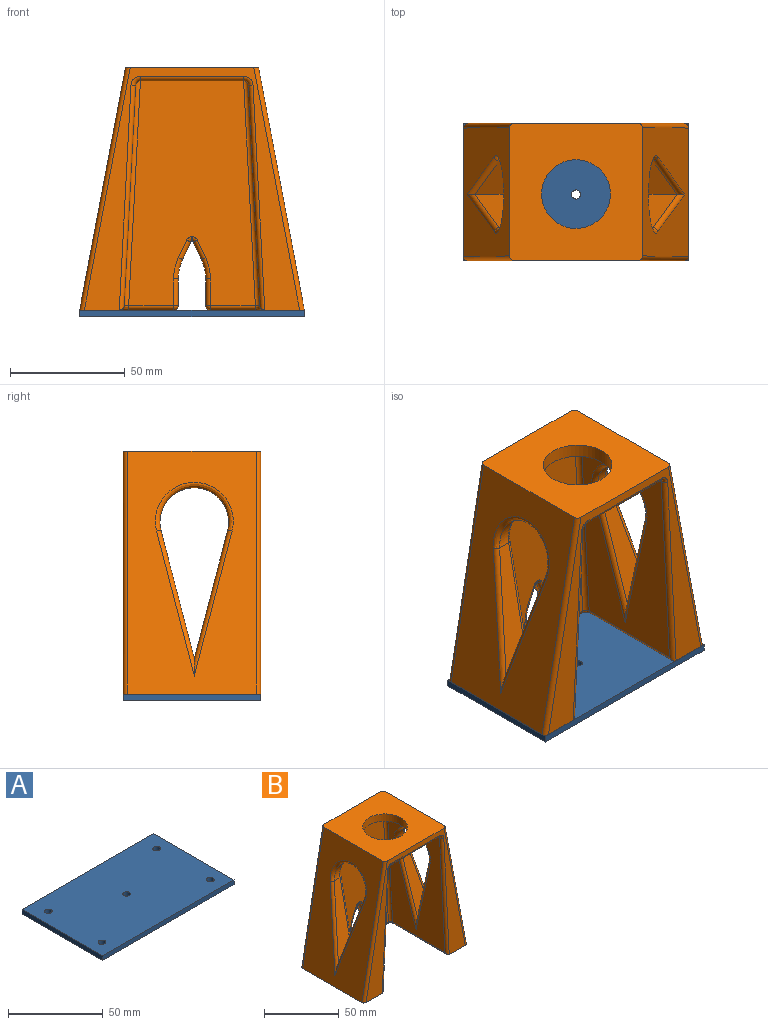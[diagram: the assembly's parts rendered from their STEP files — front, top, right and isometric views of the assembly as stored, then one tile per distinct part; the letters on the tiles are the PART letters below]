
ASSEMBLY  parts=2 mates=1
PART A: 11 faces, bbox 98x60x3 mm
  f0: plane 98x3mm, normal (0,-1,0), area 294mm2, adj f1,f3,f4,f5
  f1: plane 60x3mm, normal (1,0,0), area 180mm2, adj f0,f2,f4,f5
  f2: plane 98x3mm, normal (0,1,0), area 294mm2, adj f1,f3,f4,f5
  f3: plane 60x3mm, normal (-1,0,0), area 180mm2, adj f0,f2,f4,f5
  f4: plane 98x60mm, normal (0,0,1), area 5817.2mm2, adj f0,f1,f2,f3,f6,f7,f8,f9
  f5: plane 98x60mm, normal (0,0,-1), area 5817.2mm2, adj f0,f1,f2,f3,f6,f7,f8,f9
  f6: cylinder r=2mm len=4mm, axis (0,0,1), area 37.7mm2, adj f4,f5
  f7: cylinder r=2mm len=4mm, axis (0,0,1), area 37.7mm2, adj f4,f5
  f8: cylinder r=2mm len=4mm, axis (0,0,1), area 37.7mm2, adj f4,f5
  f9: cylinder r=2mm len=4mm, axis (0,0,1), area 37.7mm2, adj f4,f5
  f10: cylinder r=2mm len=4mm, axis (0,0,1), area 37.7mm2, adj f4,f5
PART B: 88 faces, bbox 98x60x106.7 mm
  f0: plane 98x55.27mm, normal (0,-1,0), area 4522.8mm2, adj f2,f27,f30,f39,f41,f58,f60,f62
  f1: plane 60x41mm, normal (0,0,-1), area 1096.9mm2, adj f3,f4,f18,f36,f38,f40,f41,f52
  f2: plane 51.5x45.2mm, normal (0,0,-1), area 1621.2mm2, adj f0,f5,f30,f32,f34,f37,f39
  f3: plane 106x93.93mm, normal (0,-1,0), area 1912.2mm2, adj f1,f6,f7,f31,f33,f34,f35,f36
  f4: plane 106x93.93mm, normal (0,1,0), area 7414.6mm2, adj f1,f6,f7,f59,f61,f63,f65,f67
  f5: cylinder r=15mm len=30mm, axis (0,0,-1), area 565.5mm2, adj f2,f6
  f6: plane 60x58mm, normal (0,0,1), area 2769.6mm2, adj f3,f4,f5,f17,f18,f84,f85,f86
  f7: plane 60x41mm, normal (0,0,-1), area 1096.9mm2, adj f3,f4,f17,f27,f28,f29,f31,f48
  f8: plane 11.57x2.5mm, normal (-1,0,0), area 28.9mm2, adj f15,f57,f58,f59
  f9: plane 2.5x0.04mm, normal (0,0,-1), area 0.1mm2, adj f13,f14,f66,f67
  f10: plane 11.57x2.5mm, normal (1,0,0), area 28.9mm2, adj f16,f74,f75,f77
  f11: plane 7.64x3.56mm, normal (0.91,0,-0.42), area 21.1mm2, adj f13,f16,f70,f71
  f12: plane 7.64x3.56mm, normal (-0.91,0,-0.42), area 21.1mm2, adj f14,f15,f62,f63
  f13: cylinder r=0.6mm len=2.5mm, axis (0,-1,0), area 1.7mm2, adj f9,f11,f68,f69
  f14: cylinder r=0.6mm len=2.5mm, axis (0,-1,0), area 1.7mm2, adj f9,f12,f64,f65
  f15: cylinder r=20mm len=8.45mm, axis (0,1,0), area 21.8mm2, adj f8,f12,f60,f61
  f16: cylinder r=20mm len=8.45mm, axis (0,-1,0), area 21.8mm2, adj f10,f11,f72,f73
  f17: plane 106x56mm, normal (0.98,0,0.19), area 4373.7mm2, adj f6,f7,f78,f79,f80,f86,f87
  f18: plane 106x56mm, normal (-0.98,0,0.19), area 4373.7mm2, adj f1,f6,f81,f82,f83,f84,f85
  f19: plane 55.79x16.11mm, normal (0,0.97,0.25), area 541mm2, adj f20,f21,f46,f83
  f20: cylinder r=15mm len=30mm, axis (1,0,0), area 206.6mm2, adj f19,f21,f45,f81
  f21: plane 55.79x16.11mm, normal (0,-0.97,0.25), area 541mm2, adj f19,f20,f47,f82
  f22: plane 55.79x16.11mm, normal (0,-0.97,0.25), area 541mm2, adj f23,f24,f44,f80
  f23: cylinder r=15mm len=30mm, axis (1,0,0), area 206.6mm2, adj f22,f24,f43,f79
  f24: plane 55.79x16.11mm, normal (0,0.97,0.25), area 541mm2, adj f22,f23,f42,f78
  f25: plane 96.21x49.5mm, normal (-1,0,-0.05), area 3128.5mm2, adj f29,f30,f31,f32,f42,f43,f44
  f26: plane 96.21x49.5mm, normal (1,0,-0.05), area 3128.5mm2, adj f36,f37,f38,f39,f45,f46,f47
  f27: cylinder r=2mm len=19.63mm, axis (1,0,0), area 61.7mm2, adj f0,f7,f28,f56
  f28: bspline ~4.01x4mm, area 13.3mm2, adj f7,f27,f29,f30
  f29: cylinder r=2mm len=51.5mm, axis (0,1,0), area 154.1mm2, adj f7,f25,f28,f31
  f30: cylinder r=2mm len=98.31mm, axis (-0.05,0,1), area 306.4mm2, adj f0,f2,f25,f28,f32
  f31: cylinder r=2mm len=98.31mm, axis (0.05,0,-1), area 306.7mm2, adj f3,f7,f25,f29,f33
  f32: cylinder r=2mm len=51.5mm, axis (0,1,0), area 154.1mm2, adj f2,f25,f30,f33
  f33: torus R=4mm, axis (0,-1,0), area 13mm2, adj f3,f31,f32,f34
  f34: cylinder r=2mm len=45.2mm, axis (1,0,0), area 142mm2, adj f2,f3,f33,f35
  f35: torus R=4mm, axis (0,-1,0), area 13mm2, adj f3,f34,f36,f37
  f36: cylinder r=2mm len=98.31mm, axis (0.05,0,1), area 306.7mm2, adj f1,f3,f26,f35,f38
  f37: cylinder r=2mm len=51.5mm, axis (0,-1,0), area 154.1mm2, adj f2,f26,f35,f39
  f38: cylinder r=2mm len=51.5mm, axis (0,-1,0), area 154.1mm2, adj f1,f26,f36,f40
  f39: cylinder r=2mm len=98.31mm, axis (-0.05,0,-1), area 306.4mm2, adj f0,f2,f26,f37,f40
  f40: bspline ~4.01x4mm, area 13.3mm2, adj f1,f38,f39,f41
  f41: cylinder r=2mm len=19.63mm, axis (1,0,0), area 61.7mm2, adj f0,f1,f40,f76
  f42: cylinder r=2mm len=63.83mm, axis (-0.05,-0.25,0.97), area 191.6mm2, adj f24,f25,f43,f44
  f43: bspline ~33.98x21.27mm, area 177.5mm2, adj f23,f25,f42,f44
  f44: cylinder r=2mm len=63.83mm, axis (0.05,-0.25,-0.97), area 191.6mm2, adj f22,f25,f42,f43
  f45: bspline ~33.98x21.27mm, area 177.5mm2, adj f20,f26,f46,f47
  f46: cylinder r=2mm len=63.83mm, axis (-0.05,0.25,-0.97), area 191.6mm2, adj f19,f26,f45,f47
  f47: cylinder r=2mm len=63.83mm, axis (0.05,0.25,0.97), area 191.6mm2, adj f21,f26,f45,f46
  f48: cylinder r=2.9mm len=25mm, axis (0,0,-1), area 455.5mm2, adj f7,f49
  f49: plane 5.8x5.8mm, normal (0,0,-1), area 26.4mm2, adj f48
  f50: cylinder r=2.9mm len=25mm, axis (0,0,-1), area 455.5mm2, adj f7,f51
  f51: plane 5.8x5.8mm, normal (0,0,-1), area 26.4mm2, adj f50
  f52: cylinder r=2.9mm len=25mm, axis (0,0,-1), area 455.5mm2, adj f1,f53
  f53: plane 5.8x5.8mm, normal (0,0,-1), area 26.4mm2, adj f52
  f54: cylinder r=2.9mm len=25mm, axis (0,0,-1), area 455.5mm2, adj f1,f55
  f55: plane 5.8x5.8mm, normal (0,0,-1), area 26.4mm2, adj f54
  f56: sphere r=2mm, area 6.3mm2, adj f27,f57,f58
  f57: cylinder r=2mm len=4.5mm, axis (0,1,0), area 11.9mm2, adj f7,f8,f56,f59
  f58: cylinder r=2mm len=11.57mm, axis (0,0,1), area 36.3mm2, adj f0,f8,f56,f60
  f59: cylinder r=2mm len=13.57mm, axis (0,0,1), area 40.3mm2, adj f4,f8,f57,f61
  f60: torus R=22mm, axis (0,1,0), area 28.4mm2, adj f0,f15,f58,f62
  f61: torus R=22mm, axis (0,1,0), area 28.4mm2, adj f4,f15,f59,f63
  f62: cylinder r=2mm len=8.48mm, axis (-0.42,0,0.91), area 26.5mm2, adj f0,f12,f60,f64
  f63: cylinder r=2mm len=8.48mm, axis (-0.42,0,0.91), area 26.5mm2, adj f4,f12,f61,f65
  f64: torus R=2.6mm, axis (0,1,0), area 4.7mm2, adj f0,f14,f62,f66
  f65: torus R=2.6mm, axis (0,1,0), area 4.7mm2, adj f4,f14,f63,f67
  f66: cylinder r=2mm len=2mm, axis (-1,0,0), area 0.1mm2, adj f0,f9,f64,f68
  f67: cylinder r=2mm len=2mm, axis (-1,0,0), area 0.1mm2, adj f4,f9,f65,f69
  f68: torus R=2.6mm, axis (0,1,0), area 4.7mm2, adj f0,f13,f66,f70
  f69: torus R=2.6mm, axis (0,1,0), area 4.7mm2, adj f4,f13,f67,f71
  f70: cylinder r=2mm len=8.48mm, axis (0.42,0,0.91), area 26.5mm2, adj f0,f11,f68,f72
  f71: cylinder r=2mm len=8.48mm, axis (0.42,0,0.91), area 26.5mm2, adj f4,f11,f69,f73
  f72: torus R=22mm, axis (0,1,0), area 28.4mm2, adj f0,f16,f70,f74
  f73: torus R=22mm, axis (0,1,0), area 28.4mm2, adj f4,f16,f71,f75
  f74: cylinder r=2mm len=11.57mm, axis (0,0,-1), area 36.3mm2, adj f0,f10,f72,f76
  f75: cylinder r=2mm len=13.57mm, axis (0,0,-1), area 40.3mm2, adj f4,f10,f73,f77
  f76: sphere r=2mm, area 6.3mm2, adj f41,f74,f77
  f77: cylinder r=2mm len=4.5mm, axis (0,-1,0), area 11.9mm2, adj f1,f10,f75,f76
  f78: cylinder r=2mm len=63.47mm, axis (-0.18,-0.25,0.95), area 187.5mm2, adj f17,f24,f79,f80
  f79: bspline ~33.98x21.27mm, area 193.2mm2, adj f17,f23,f78,f80
  f80: cylinder r=2mm len=63.47mm, axis (0.18,-0.25,-0.95), area 187.5mm2, adj f17,f22,f78,f79
  f81: bspline ~33.98x21.27mm, area 193.2mm2, adj f18,f20,f82,f83
  f82: cylinder r=2mm len=63.47mm, axis (0.18,0.25,0.95), area 187.5mm2, adj f18,f21,f81,f83
  f83: cylinder r=2mm len=63.47mm, axis (-0.18,0.25,-0.95), area 187.5mm2, adj f18,f19,f81,f82
  f84: cylinder r=2mm len=106.74mm, axis (0.19,0,0.98), area 338.9mm2, adj f1,f4,f6,f18
  f85: cylinder r=2mm len=106.74mm, axis (0.19,0,0.98), area 338.9mm2, adj f1,f3,f6,f18
  f86: cylinder r=2mm len=106.74mm, axis (0.19,0,-0.98), area 338.9mm2, adj f4,f6,f7,f17
  f87: cylinder r=2mm len=106.74mm, axis (0.19,0,-0.98), area 338.9mm2, adj f3,f6,f7,f17
PLACE A rot(axis=(0,0,1),180deg) t=(-2.83,34.9,4.79)mm
PLACE B t=(-2.83,33.9,107.79)mm
MATE fastened A.f8 <-> B.f52  axis (0,0,1) through (-43.2,55.9,7.79)mm
